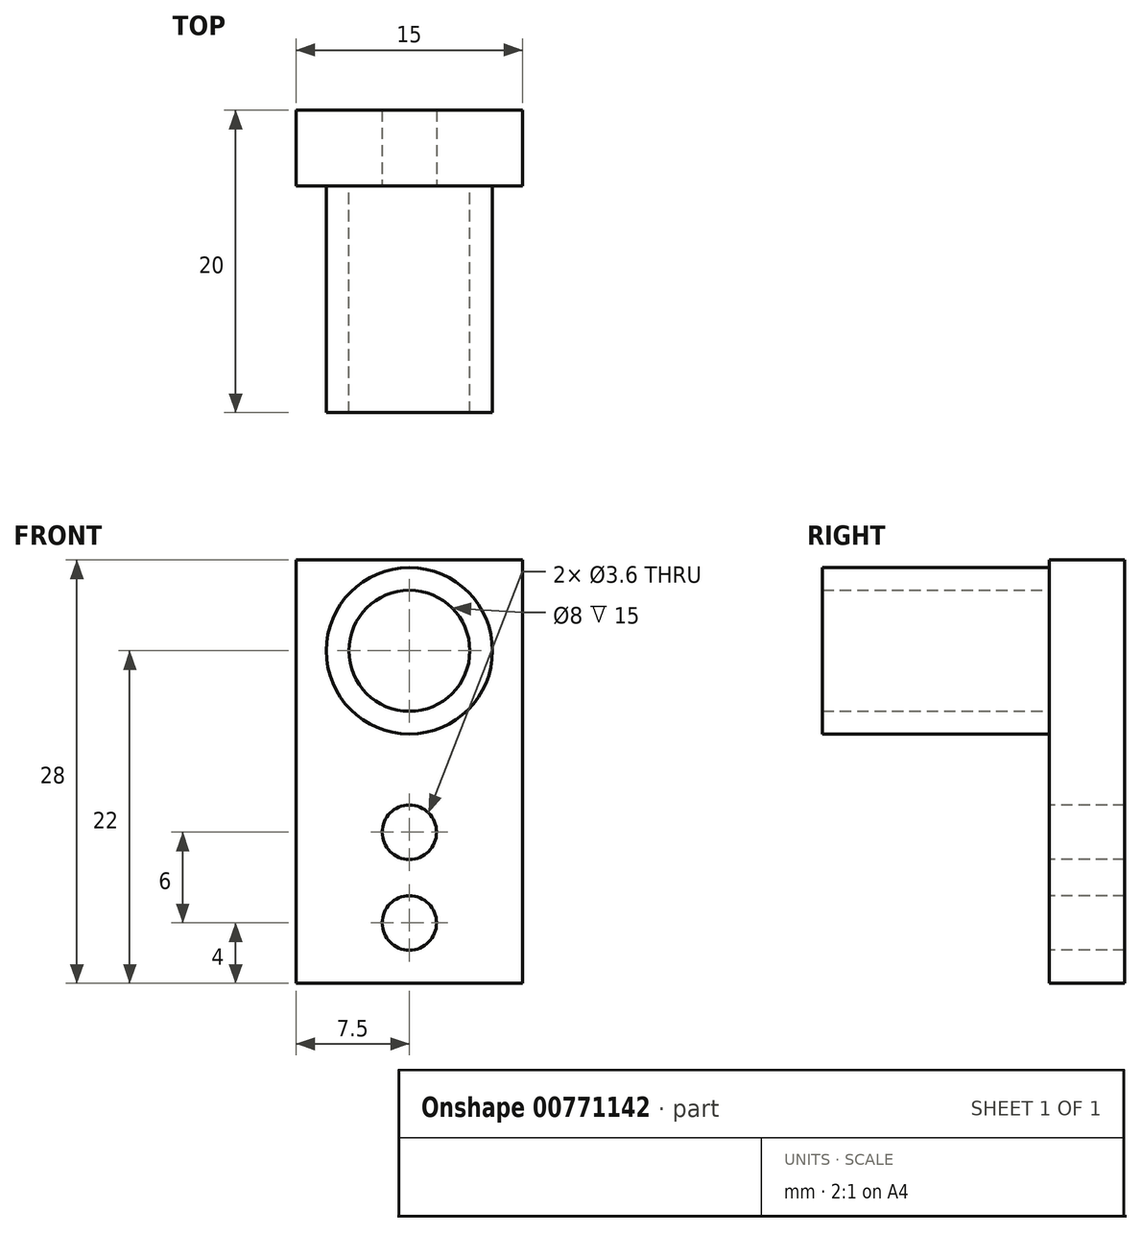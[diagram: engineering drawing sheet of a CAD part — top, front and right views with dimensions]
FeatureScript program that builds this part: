
annotation { "Feature Type Name" : "Feature", "Feature Type Description" : "" }
export const myFeature = defineFeature(function(context is Context, id is Id, definition is map)
    precondition{}
    {
        {
            var Q0;
            Q0=qCreatedBy(makeId("Front.planeOp"),FACE);
            var sketch = newSketch(context, id + "F0", { "sketchPlane" : qUnion([Q0])});
            skLineSegment(sketch, "E0.bottom", {"start": v(7.5, -14) * mm, "end": v(-7.5, -14) * mm});
            skLineSegment(sketch, "E0.top", {"start": v(7.5, 14) * mm, "end": v(-7.5, 14) * mm});
            skLineSegment(sketch, "E0.left", {"start": v(7.5, -14) * mm, "end": v(7.5, 14) * mm});
            skLineSegment(sketch, "E0.right", {"start": v(-7.5, -14) * mm, "end": v(-7.5, 14) * mm});
            skPoint(sketch, "E0.middle", {"position": v(0, 0) * mm});
            skCircle(sketch, "E1", {"center": v(0, 8) * mm, "radius": 4 * mm});
            skCircle(sketch, "E2", {"center": v(0, 8) * mm, "radius": 5.5 * mm});
            skCircle(sketch, "E3", {"center": v(0, -4) * mm, "radius": 1.8 * mm});
            skCircle(sketch, "E4", {"center": v(0, -10) * mm, "radius": 1.8 * mm});
            skSolve(sketch);
        }
        {
            var Q0;
            Q0=makeQuery(id+"F0.imprint","IMPRINT",FACE,{"disambiguationData":[TD([[makeQuery(id+"F0.imprint","IMPRINT",EDGE,{"derivedFrom":sQuery(id+"F0.wireOp",EDGE,"E0.bottom")}),-1.0]])]});
            var Q1;
            Q1=makeQuery(id+"F0.imprint","IMPRINT",FACE,{"disambiguationData":[TD([[makeQuery(id+"F0.imprint","IMPRINT",EDGE,{"derivedFrom":sQuery(id+"F0.wireOp",EDGE,"E1")}),1.0]])]});
            var Q2;
            Q2=makeQuery(id+"F0.imprint","IMPRINT",FACE,{"disambiguationData":[TD([[makeQuery(id+"F0.imprint","IMPRINT",EDGE,{"derivedFrom":sQuery(id+"F0.wireOp",EDGE,"E1")}),-1.0]])]});
            extrude(context, id + "F1", {"entities" : qUnion([Q0, Q1, Q2]), "oppositeDirection" : true, "depth" : 5 * mm, "offsetDistance" : 25 * mm});
        }
        {
            var Q0;
            Q0=makeQuery(id+"F0.imprint","IMPRINT",FACE,{"disambiguationData":[TD([[makeQuery(id+"F0.imprint","IMPRINT",EDGE,{"derivedFrom":sQuery(id+"F0.wireOp",EDGE,"E1")}),-1.0]])]});
            extrude(context, id + "F2", {"entities" : qUnion([Q0]), "operationType" : NewBodyOperationType.ADD, "depth" : 15 * mm, "offsetDistance" : 25 * mm});
        }
    });
